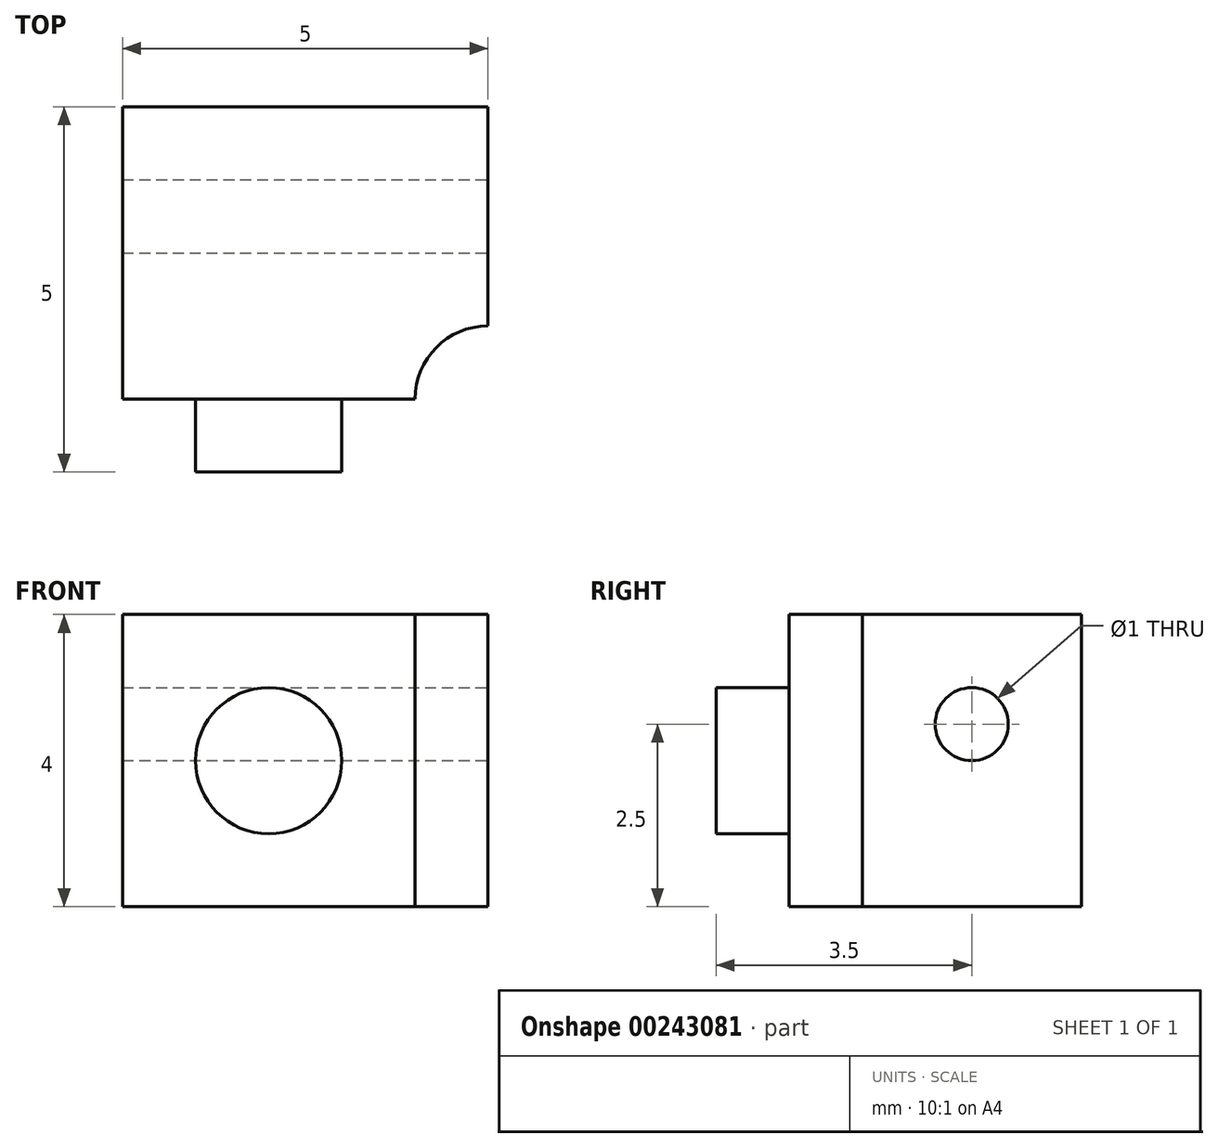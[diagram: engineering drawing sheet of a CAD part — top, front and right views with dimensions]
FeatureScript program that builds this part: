
annotation { "Feature Type Name" : "Feature", "Feature Type Description" : "" }
export const myFeature = defineFeature(function(context is Context, id is Id, definition is map)
    precondition{}
    {
        {
            var Q0;
            Q0=qCreatedBy(makeId("Top.planeOp"),FACE);
            var sketch = newSketch(context, id + "F0", { "sketchPlane" : qUnion([Q0])});
            skLineSegment(sketch, "E0.bottom", {"start": v(0, 0) * mm, "end": v(5, 0) * mm});
            skLineSegment(sketch, "E0.top", {"start": v(0, 4) * mm, "end": v(5, 4) * mm});
            skLineSegment(sketch, "E0.left", {"start": v(0, 0) * mm, "end": v(0, 4) * mm});
            skLineSegment(sketch, "E0.right", {"start": v(5, 0) * mm, "end": v(5, 4) * mm});
            skSolve(sketch);
        }
        {
            var Q0;
            Q0 = qSketchRegion(id + "F0", true);
            extrude(context, id + "F1", {"entities" : qUnion([Q0]), "depth" : 4 * mm});
        }
        {
            var Q0;
            Q0=makeQuery(id+"F1.opExtrude","SWEPT_FACE",FACE,{"disambiguationData":[OSD([sQuery(id+"F0.wireOp",EDGE,"E0.bottom")])]});
            var sketch = newSketch(context, id + "F2", { "sketchPlane" : qUnion([Q0])});
            skCircle(sketch, "E1", {"center": v(2, 2) * mm, "radius": 1 * mm});
            skPoint(sketch, "E1.centerSnap0", {"position": v(0, 2) * mm});
            skSolve(sketch);
        }
        {
            var Q0;
            Q0 = qSketchRegion(id + "F2", true);
            extrude(context, id + "F3", {"entities" : qUnion([Q0]), "operationType" : NewBodyOperationType.ADD, "depth" : 1 * mm});
        }
        {
            var Q0;
            Q0=makeQuery(id+"F1.opExtrude","CAP_FACE",FACE,{"disambiguationData":[OSD([sQuery(id+"F0.wireOp",EDGE,"E0.bottom"),sQuery(id+"F0.wireOp",EDGE,"E0.top"),sQuery(id+"F0.wireOp",EDGE,"E0.left"),sQuery(id+"F0.wireOp",EDGE,"E0.right")])],"isStart":false});
            var sketch = newSketch(context, id + "F4", { "sketchPlane" : qUnion([Q0])});
            skArc(sketch, "E2", {"start": v(5, 1) * mm, "mid": v(4.3, 0.7) * mm, "end": v(4, 0) * mm});
            skLineSegment(sketch, "E3", {"start": v(5, 1) * mm, "end": v(5, 0) * mm});
            skLineSegment(sketch, "E4", {"start": v(4, 0) * mm, "end": v(5, 0) * mm});
            skSolve(sketch);
        }
        {
            var Q0;
            Q0 = qSketchRegion(id + "F4", true);
            extrude(context, id + "F5", {"entities" : qUnion([Q0]), "operationType" : NewBodyOperationType.REMOVE, "oppositeDirection" : true, "depth" : 4 * mm});
        }
        {
            var Q0;
            Q0=makeQuery(id+"F1.opExtrude","SWEPT_FACE",FACE,{"disambiguationData":[OSD([sQuery(id+"F0.wireOp",EDGE,"E0.right")])]});
            var sketch = newSketch(context, id + "F6", { "sketchPlane" : qUnion([Q0])});
            skCircle(sketch, "E5", {"center": v(2.5, 2.5) * mm, "radius": 0.5 * mm});
            skPoint(sketch, "E5.centerSnap0", {"position": v(2.5, 4) * mm});
            skSolve(sketch);
        }
        {
            var Q0;
            Q0 = qSketchRegion(id + "F6", true);
            extrude(context, id + "F7", {"entities" : qUnion([Q0]), "operationType" : NewBodyOperationType.REMOVE, "oppositeDirection" : true, "depth" : 5 * mm});
        }
    });
